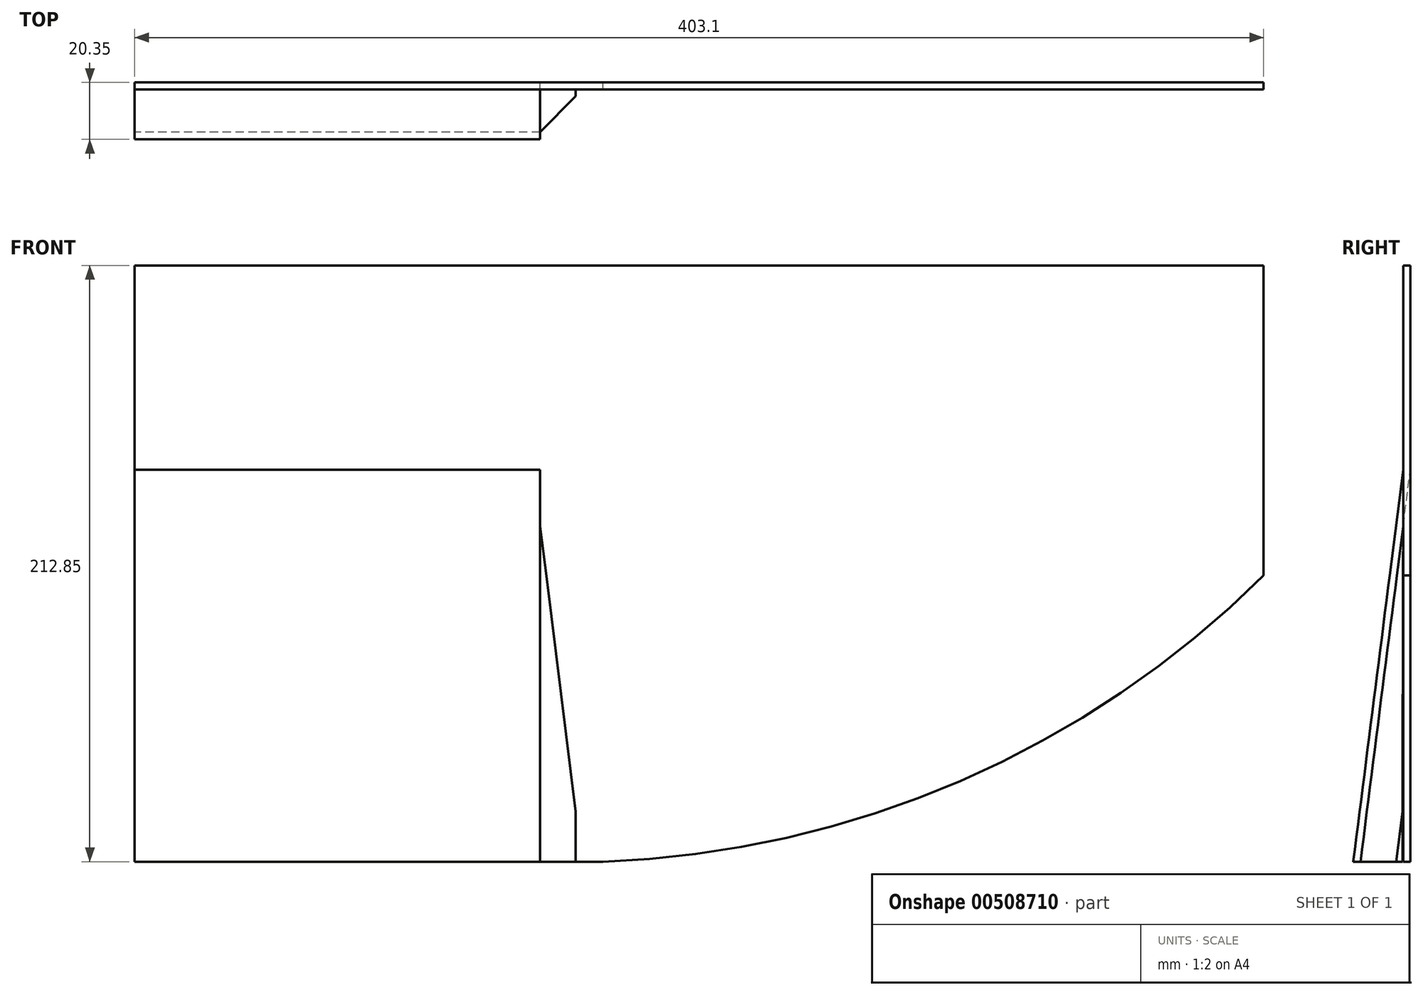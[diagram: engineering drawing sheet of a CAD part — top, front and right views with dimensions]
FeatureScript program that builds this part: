
annotation { "Feature Type Name" : "Feature", "Feature Type Description" : "" }
export const myFeature = defineFeature(function(context is Context, id is Id, definition is map)
    precondition{}
    {
        {
            var Q0;
            Q0=qCreatedBy(makeId("Front.planeOp"),FACE);
            var sketch = newSketch(context, id + "F0", { "sketchPlane" : qUnion([Q0])});
            skLineSegment(sketch, "E0", {"start": v(-60.7, 186.23) * mm, "end": v(342.4, 186.23) * mm});
            skLineSegment(sketch, "E1", {"start": v(342.4, 186.23) * mm, "end": v(342.4, -26.62) * mm});
            skLineSegment(sketch, "E2", {"start": v(342.4, -26.62) * mm, "end": v(-60.7, -26.62) * mm});
            skLineSegment(sketch, "E3", {"start": v(-60.7, -26.62) * mm, "end": v(-60.7, 186.23) * mm});
            skPoint(sketch, "E4", {"position": v(81.54, -26.62) * mm});
            skPoint(sketch, "E5", {"position": v(342.4, 75.59) * mm});
            skArc(sketch, "E6", {"start": v(81.54, -26.62) * mm, "mid": v(222.57, -2.56) * mm, "end": v(342.4, 75.59) * mm});
            skSolve(sketch);
        }
        {
            var Q0;
            {var subQ5=sQuery(id+"F0.wireOp",EDGE,"E0");Q0=makeQuery(id+"F0.imprint","IMPRINT",FACE,{"disambiguationData":[TD([[makeQuery(id+"F0.imprint","IMPRINT",EDGE,{"derivedFrom":subQ5}),-1.0]])]});}
            extrude(context, id + "F1", {"entities" : qUnion([Q0]), "depth" : 25.4 * mm});
        }
        {
            var Q0;
            Q0=makeQuery(id+"F1.opExtrude","SWEPT_FACE",FACE,{"disambiguationData":[OSD([sQuery(id+"F0.wireOp",EDGE,"E3")])]});
            var sketch = newSketch(context, id + "F2", { "sketchPlane" : qUnion([Q0])});
            skLineSegment(sketch, "E7", {"start": v(17.78, -26.62) * mm, "end": v(0, 113.08) * mm});
            skLineSegment(sketch, "E8", {"start": v(2.54, 186.23) * mm, "end": v(2.54, 113.3) * mm});
            skLineSegment(sketch, "E9", {"start": v(2.54, 113.3) * mm, "end": v(20.35, -26.62) * mm});
            skLineSegment(sketch, "E10", {"start": v(20.35, -26.62) * mm, "end": v(17.78, -26.62) * mm});
            skSolve(sketch);
        }
        {
            var Q0;
            Q0=makeQuery(id+"F1.opExtrude","SWEPT_FACE",FACE,{"disambiguationData":[OSD([sQuery(id+"F0.wireOp",EDGE,"E1")])]});
            var sketch = newSketch(context, id + "F3", { "sketchPlane" : qUnion([Q0])});
            skLineSegment(sketch, "E11", {"start": v(0, 112.97) * mm, "end": v(-2.54, 112.97) * mm});
            skLineSegment(sketch, "E12", {"start": v(-2.54, 112.97) * mm, "end": v(-2.54, -26.73) * mm});
            skLineSegment(sketch, "E13", {"start": v(-2.54, -26.73) * mm, "end": v(0, -26.73) * mm});
            skLineSegment(sketch, "E14", {"start": v(0, -26.73) * mm, "end": v(0, 112.97) * mm});
            skLineSegment(sketch, "E15", {"start": v(-2.54, 112.97) * mm, "end": v(-2.54, 186.23) * mm});
            skLineSegment(sketch, "E16", {"start": v(-2.54, 186.23) * mm, "end": v(0, 186.23) * mm});
            skLineSegment(sketch, "E17", {"start": v(0, 186.23) * mm, "end": v(0, 112.97) * mm});
            skSolve(sketch);
        }
        {
            var Q0;
            {var subQ4=sQuery(id+"F2.wireOp",EDGE,"E8");Q0=makeQuery(id+"F2.imprint","IMPRINT",FACE,{"disambiguationData":[TD([[makeQuery(id+"F2.imprint","IMPRINT",EDGE,{"derivedFrom":subQ4}),1.0]])]});}
            extrude(context, id + "F4", {"entities" : qUnion([Q0]), "operationType" : NewBodyOperationType.REMOVE, "oppositeDirection" : true, "depth" : 144.78 * mm});
        }
        {
            var Q0;
            {var subQ0=sQuery(id+"F2.wireOp",EDGE,"E7");Q0=makeQuery(id+"F2.imprint","IMPRINT",FACE,{"disambiguationData":[TD([[makeQuery(id+"F2.imprint","IMPRINT",EDGE,{"derivedFrom":subQ0}),1.0]])]});}
            extrude(context, id + "F5", {"entities" : qUnion([Q0]), "operationType" : NewBodyOperationType.REMOVE, "oppositeDirection" : true, "depth" : 144.78 * mm});
        }
        {
            var Q0;
            {var subQ3=sQuery(id+"F3.wireOp",EDGE,"E15");Q0=makeQuery(id+"F3.imprint","IMPRINT",FACE,{"disambiguationData":[TD([[makeQuery(id+"F3.imprint","IMPRINT",EDGE,{"derivedFrom":subQ3}),1.0]])]});}
            extrude(context, id + "F6", {"entities" : qUnion([Q0]), "operationType" : NewBodyOperationType.REMOVE, "oppositeDirection" : true, "depth" : 258.32 * mm});
        }
        {
            var Q0;
            Q0=makeQuery(id+"F6.boolean.opBoolean","COPY",FACE,{"derivedFrom":makeQuery(id+"F6.opExtrude","SWEPT_FACE",FACE,{"disambiguationData":[OSD([sQuery(id+"F0.wireOp",EDGE,"E1"),sQuery(id+"F0.wireOp",EDGE,"E6")])]})});
            var sketch = newSketch(context, id + "F7", { "sketchPlane" : qUnion([Q0])});
            skLineSegment(sketch, "E18", {"start": v(84.08, -2.54) * mm, "end": v(84.08, -25.4) * mm});
            skLineSegment(sketch, "E19", {"start": v(84.08, -25.4) * mm, "end": v(342.4, -25.4) * mm});
            skLineSegment(sketch, "E20", {"start": v(342.4, -25.4) * mm, "end": v(342.4, -2.54) * mm});
            skLineSegment(sketch, "E21", {"start": v(342.4, -2.54) * mm, "end": v(84.08, -2.54) * mm});
            skSolve(sketch);
        }
        {
            var Q0;
            {var subQ0=sQuery(id+"F7.wireOp",EDGE,"E19");Q0=makeQuery(id+"F7.imprint","IMPRINT",FACE,{"disambiguationData":[TD([[makeQuery(id+"F7.imprint","IMPRINT",EDGE,{"derivedFrom":subQ0}),1.0]])]});}
            extrude(context, id + "F8", {"entities" : qUnion([Q0]), "operationType" : NewBodyOperationType.REMOVE, "oppositeDirection" : true, "depth" : 152.4 * mm});
        }
        {
            var Q0;
            Q0=makeQuery(id+"F8.boolean.opBoolean","MERGE",FACE,{"derivedFrom":[makeQuery(id+"F6.boolean.opBoolean","COPY",FACE,{"derivedFrom":makeQuery(id+"F6.opExtrude","CAP_FACE",FACE,{"disambiguationData":[OSD([sQuery(id+"F0.wireOp",EDGE,"E0"),sQuery(id+"F0.wireOp",EDGE,"E1"),sQuery(id+"F0.wireOp",EDGE,"E6"),sQuery(id+"F3.wireOp",EDGE,"E12"),sQuery(id+"F3.wireOp",EDGE,"E15")])],"isStart":false})}),makeQuery(id+"F8.opExtrude","SWEPT_FACE",FACE,{"disambiguationData":[OSD([sQuery(id+"F7.wireOp",EDGE,"E18")])]})]});
            var sketch = newSketch(context, id + "F9", { "sketchPlane" : qUnion([Q0])});
            skLineSegment(sketch, "E22", {"start": v(-20.35, -26.62) * mm, "end": v(-2.74, -26.62) * mm});
            skPoint(sketch, "E22.endSnap0", {"position": v(-19.06, -26.62) * mm});
            skLineSegment(sketch, "E23", {"start": v(-2.74, -26.62) * mm, "end": v(-2.54, 93.12) * mm});
            skLineSegment(sketch, "E24", {"start": v(-2.54, 93.12) * mm, "end": v(-20.35, -26.62) * mm});
            skSolve(sketch);
        }
        {
            var Q0;
            {var subQ10=sQuery(id+"F9.wireOp",EDGE,"E23");Q0=makeQuery(id+"F9.imprint","IMPRINT",FACE,{"disambiguationData":[TD([[makeQuery(id+"F9.imprint","IMPRINT",EDGE,{"derivedFrom":subQ10}),1.0]])]});}
            extrude(context, id + "F10", {"entities" : qUnion([Q0]), "depth" : 12.7 * mm});
        }
        {
            var Q0;
            {var subQ2=sQuery(id+"F2.wireOp",EDGE,"E7");var subQ3=makeQuery(id+"F5.boolean.opBoolean","COPY",FACE,{"derivedFrom":makeQuery(id+"F5.opExtrude","SWEPT_FACE",FACE,{"disambiguationData":[OSD([subQ2])]})});var subQ4=sQuery(id+"F0.wireOp",EDGE,"E2");var subQ5=makeQuery(id+"F5.boolean.opBoolean","COPY",FACE,{"derivedFrom":makeQuery(id+"F5.opExtrude","CAP_FACE",FACE,{"disambiguationData":[OSD([subQ4,sQuery(id+"F0.wireOp",EDGE,"E3"),subQ2])],"isStart":false})});Q0=makeQuery(id+"F10.opExtrude","CAP_EDGE",EDGE,{"disambiguationData":[OSD([subQ2]),TDD([makeQuery(id+"F9.imprint","IMPRINT",EDGE,{"derivedFrom":makeQuery(id+"F6.boolean.opBoolean","SPLIT",EDGE,{"disambiguationData":[topologyDisambiguationEdgeConnected([subQ3,subQ5]),TD([makeQuery(id+"F1.opExtrude","SWEPT_FACE",FACE,{"disambiguationData":[OSD([subQ4])]})])],"derivedFrom":makeQuery(id+"F5.boolean.opBoolean","COPY",EDGE,{"derivedFrom":makeQuery(id+"F5.opExtrude","CAP_EDGE",EDGE,{"disambiguationData":[OSD([subQ2])],"isStart":false})})})})])],"isStart":false});}
            chamfer(context, id + "F11", {"entities" : qUnion([Q0]), "width" : 12.7 * mm, "tangentPropagation" : true});
        }
    });
